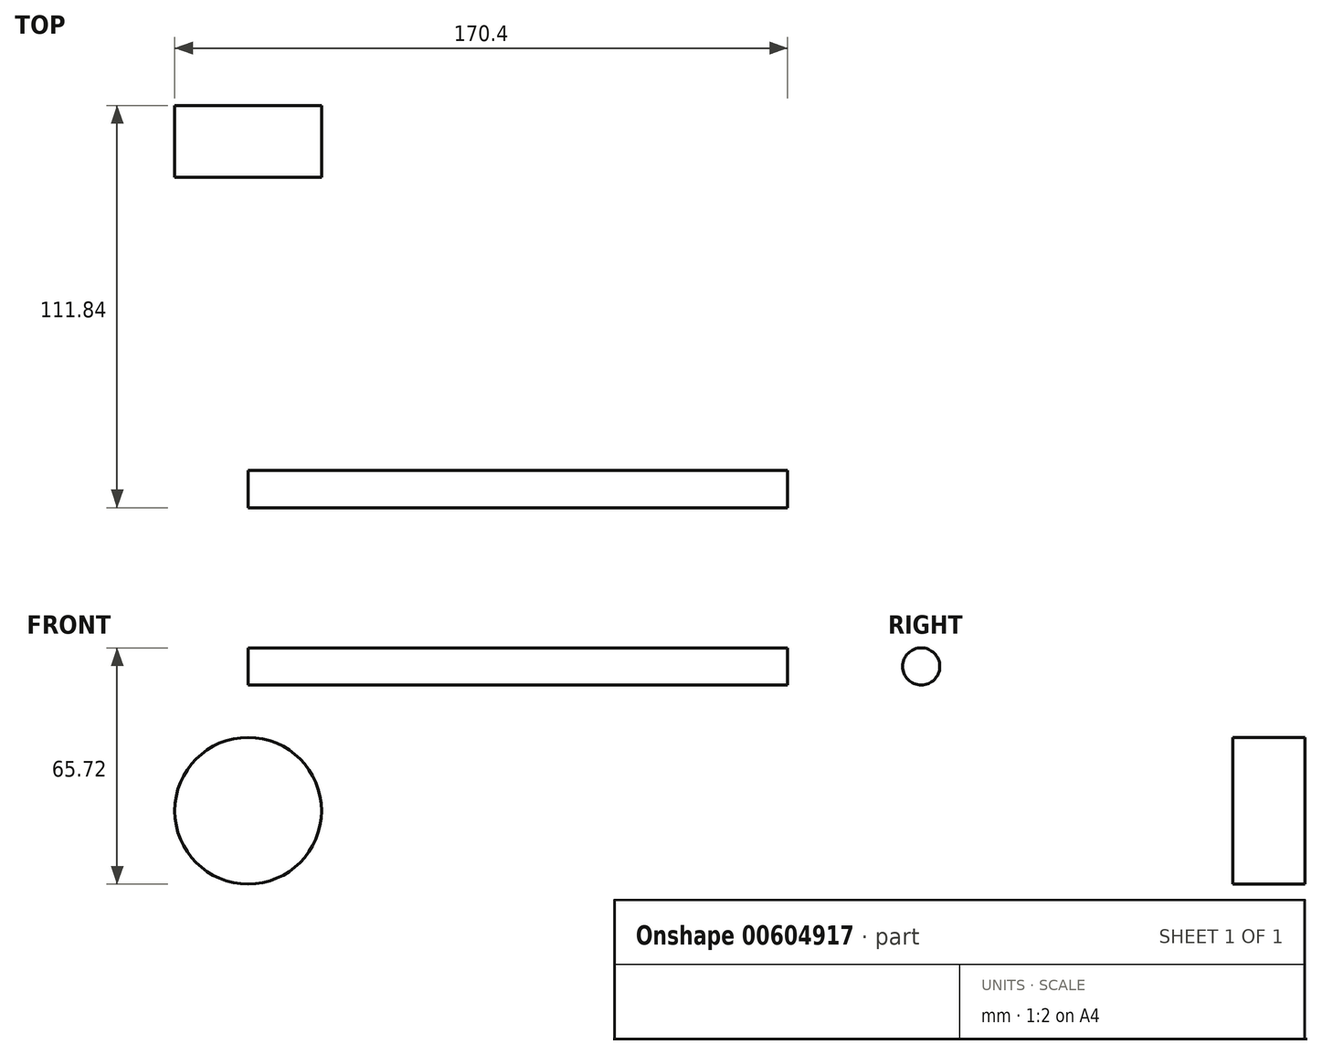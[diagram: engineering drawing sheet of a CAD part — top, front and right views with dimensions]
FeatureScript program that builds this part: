
annotation { "Feature Type Name" : "Feature", "Feature Type Description" : "" }
export const myFeature = defineFeature(function(context is Context, id is Id, definition is map)
    precondition{}
    {
        {
            var Q0;
            Q0=qCreatedBy(makeId("Front.planeOp"),FACE);
            var sketch = newSketch(context, id + "F0", { "sketchPlane" : qUnion([Q0])});
            skCircle(sketch, "E0", {"center": v(0, 0) * mm, "radius": 20.4 * mm});
            skSolve(sketch);
        }
        {
            var Q0;
            Q0=makeQuery(id+"F0.imprint","IMPRINT",FACE,{"disambiguationData":[TD([[makeQuery(id+"F0.imprint","IMPRINT",EDGE,{"derivedFrom":sQuery(id+"F0.wireOp",EDGE,"E0")}),1.0]])]});
            extrude(context, id + "F1", {"entities" : qUnion([Q0]), "depth" : 20 * mm, "offsetDistance" : 25 * mm});
        }
        {
            var Q0;
            Q0=qCreatedBy(makeId("Right.planeOp"),FACE);
            var sketch = newSketch(context, id + "F2", { "sketchPlane" : qUnion([Q0])});
            skCircle(sketch, "E1", {"center": v(-106.67, 40.15) * mm, "radius": 5.17 * mm});
            skSolve(sketch);
        }
        {
            var Q0;
            Q0 = qSketchRegion(id + "F2", true);
            extrude(context, id + "F3", {"entities" : qUnion([Q0]), "depth" : 150 * mm, "offsetDistance" : 25 * mm});
        }
    });
